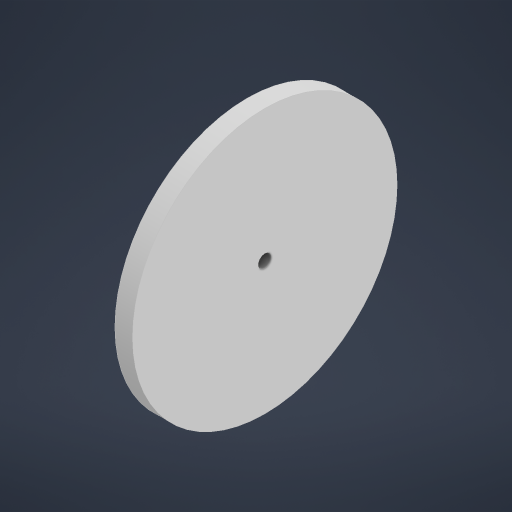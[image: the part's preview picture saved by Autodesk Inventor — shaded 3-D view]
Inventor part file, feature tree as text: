
AUTODESK INVENTOR PART (.ipt)
format: ipt  version: 2023.2 (Build 272271000, 271)  size: 247,808 bytes
history: native  units: mm
features: sketch x1
ambient origin geometry x8: Origin, YZ Plane, XZ Plane, XY Plane, X Axis, Y Axis, Z Axis, Center Point
bodies: Body1 (feature_tree)
feature tree (1):
  sketch  "Sketch1"  dims[d228=60.0mm d229=4.0mm d230=0.0mm d231=3.0mm d232=6.0mm d233=4.0mm d234=2.0mm d235=90.0deg d236=8.0mm d237=20.594885mm d9=0.5mm d10=0.872665mm d11=0.5mm d12=0.872665mm d13=0.5mm d14=0.872665mm d27=0.5mm d28=0.872665mm d29=0.5mm d30=0.872665mm d88=0.5mm d89=0.872665mm d90=0.5mm d91=0.872665mm d116=0.5mm d117=0.872665mm d118=0.5mm d119=0.872665mm d154=0.5mm d155=0.872665mm d156=0.5mm d157=0.872665mm d181=0.5mm d182=0.872665mm d183=0.5mm d184=0.872665mm d221=0.5mm d222=0.872665mm d223=0.5mm d224=0.872665mm]
